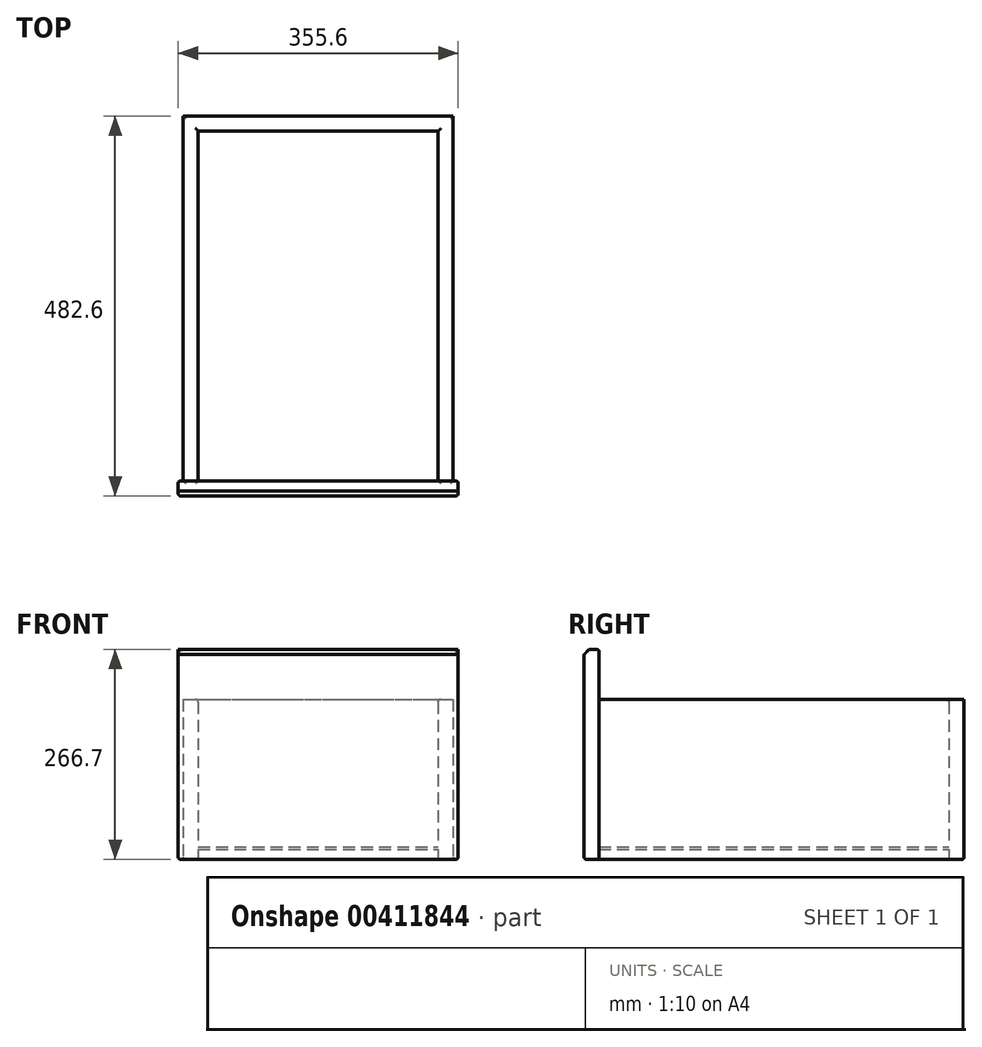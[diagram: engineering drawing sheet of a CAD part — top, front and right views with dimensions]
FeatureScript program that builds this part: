
annotation { "Feature Type Name" : "Feature", "Feature Type Description" : "" }
export const myFeature = defineFeature(function(context is Context, id is Id, definition is map)
    precondition{}
    {
        {
            var Q0;
            Q0=qCreatedBy(makeId("Top.planeOp"),FACE);
            var sketch = newSketch(context, id + "F0", { "sketchPlane" : qUnion([Q0])});
            skLineSegment(sketch, "E0.bottom", {"start": v(0, 0) * mm, "end": v(19.05, 0) * mm});
            skLineSegment(sketch, "E0.top", {"start": v(0, 463.55) * mm, "end": v(342.9, 463.55) * mm});
            skLineSegment(sketch, "E0.left", {"start": v(0, 0) * mm, "end": v(0, 463.55) * mm});
            skLineSegment(sketch, "E0.right", {"start": v(342.9, 0) * mm, "end": v(342.9, 463.55) * mm});
            skLineSegment(sketch, "E1.top", {"start": v(19.05, 444.5) * mm, "end": v(323.85, 444.5) * mm});
            skLineSegment(sketch, "E1.left", {"start": v(19.05, 0) * mm, "end": v(19.05, 444.5) * mm});
            skLineSegment(sketch, "E1.right", {"start": v(323.85, 0) * mm, "end": v(323.85, 444.5) * mm});
            skLineSegment(sketch, "E2.trimOffspring", {"start": v(323.85, 0) * mm, "end": v(342.9, 0) * mm});
            skSolve(sketch);
        }
        {
            var Q0;
            Q0=makeQuery(id+"F0.imprint","IMPRINT",FACE,{"disambiguationData":[TD([[makeQuery(id+"F0.imprint","IMPRINT",EDGE,{"derivedFrom":sQuery(id+"F0.wireOp",EDGE,"E0.bottom")}),1.0]])]});
            extrude(context, id + "F1", {"entities" : qUnion([Q0]), "depth" : 203.2 * mm});
        }
        {
            var Q0;
            Q0=qCreatedBy(makeId("Top.planeOp"),FACE);
            var sketch = newSketch(context, id + "F2", { "sketchPlane" : qUnion([Q0])});
            skLineSegment(sketch, "E3.bottom", {"start": v(-6.35, 0) * mm, "end": v(349.25, 0) * mm});
            skLineSegment(sketch, "E3.top", {"start": v(-6.35, -19.05) * mm, "end": v(349.25, -19.05) * mm});
            skLineSegment(sketch, "E3.left", {"start": v(-6.35, 0) * mm, "end": v(-6.35, -19.05) * mm});
            skLineSegment(sketch, "E3.right", {"start": v(349.25, 0) * mm, "end": v(349.25, -19.05) * mm});
            skSolve(sketch);
        }
        {
            var Q0;
            Q0 = qSketchRegion(id + "F2", true);
            extrude(context, id + "F3", {"entities" : qUnion([Q0]), "operationType" : NewBodyOperationType.ADD, "depth" : 266.7 * mm});
        }
        {
            var Q0;
            Q0=makeQuery(id+"F3.opExtrude","CAP_EDGE",EDGE,{"disambiguationData":[OSD([sQuery(id+"F2.wireOp",EDGE,"E3.top")])],"isStart":false});
            chamfer(context, id + "F4", {"entities" : qUnion([Q0]), "width" : 6.35 * mm, "tangentPropagation" : true});
        }
        {
            var Q0;
            Q0=makeQuery(id+"F3.opExtrude","SWEPT_EDGE",EDGE,{"disambiguationData":[OSD([sQuery(id+"F2.wireOp",EDGE,"E3.top"),sQuery(id+"F2.wireOp",EDGE,"E3.left")])]});
            var Q1;
            Q1=makeQuery(id+"F3.opExtrude","SWEPT_EDGE",EDGE,{"disambiguationData":[OSD([sQuery(id+"F2.wireOp",EDGE,"E3.bottom"),sQuery(id+"F2.wireOp",EDGE,"E3.left")])]});
            var Q2;
            {var subQ0=sQuery(id+"F2.wireOp",EDGE,"E3.bottom");var subQ2=sQuery(id+"F0.wireOp",EDGE,"E1.left");Q2=makeQuery(id+"F3.boolean.opBoolean","SPLIT",EDGE,{"disambiguationData":[TD([makeQuery(id+"F1.opExtrude","SWEPT_FACE",FACE,{"disambiguationData":[OSD([subQ2])]})])],"derivedFrom":makeQuery(id+"F3.opExtrude","CAP_EDGE",EDGE,{"disambiguationData":[OSD([subQ0])],"isStart":true})});}
            var Q3;
            Q3=makeQuery(id+"F3.opExtrude","CAP_EDGE",EDGE,{"disambiguationData":[OSD([sQuery(id+"F2.wireOp",EDGE,"E3.top")])],"isStart":true});
            var Q4;
            Q4=makeQuery(id+"F1.opExtrude","CAP_EDGE",EDGE,{"disambiguationData":[OSD([sQuery(id+"F0.wireOp",EDGE,"E0.left")])],"isStart":true});
            var Q5;
            Q5=makeQuery(id+"F1.opExtrude","CAP_EDGE",EDGE,{"disambiguationData":[OSD([sQuery(id+"F0.wireOp",EDGE,"E1.left")])],"isStart":true});
            var Q6;
            Q6=makeQuery(id+"F1.opExtrude","CAP_EDGE",EDGE,{"disambiguationData":[OSD([sQuery(id+"F0.wireOp",EDGE,"E0.top")])],"isStart":true});
            var Q7;
            Q7=makeQuery(id+"F1.opExtrude","CAP_EDGE",EDGE,{"disambiguationData":[OSD([sQuery(id+"F0.wireOp",EDGE,"E1.top")])],"isStart":true});
            var Q8;
            Q8=makeQuery(id+"F1.opExtrude","CAP_EDGE",EDGE,{"disambiguationData":[OSD([sQuery(id+"F0.wireOp",EDGE,"E1.right")])],"isStart":true});
            var Q9;
            Q9=makeQuery(id+"F1.opExtrude","CAP_EDGE",EDGE,{"disambiguationData":[OSD([sQuery(id+"F0.wireOp",EDGE,"E0.right")])],"isStart":true});
            var Q10;
            Q10=makeQuery(id+"F3.opExtrude","SWEPT_EDGE",EDGE,{"disambiguationData":[OSD([sQuery(id+"F2.wireOp",EDGE,"E3.bottom"),sQuery(id+"F2.wireOp",EDGE,"E3.right")])]});
            var Q11;
            Q11=makeQuery(id+"F3.opExtrude","SWEPT_EDGE",EDGE,{"disambiguationData":[OSD([sQuery(id+"F2.wireOp",EDGE,"E3.top"),sQuery(id+"F2.wireOp",EDGE,"E3.right")])]});
            var Q12;
            Q12=makeQuery(id+"F1.opExtrude","CAP_EDGE",EDGE,{"disambiguationData":[OSD([sQuery(id+"F0.wireOp",EDGE,"E1.left")])],"isStart":false});
            var Q13;
            Q13=makeQuery(id+"F1.opExtrude","CAP_EDGE",EDGE,{"disambiguationData":[OSD([sQuery(id+"F0.wireOp",EDGE,"E1.top")])],"isStart":false});
            var Q14;
            Q14=makeQuery(id+"F1.opExtrude","CAP_EDGE",EDGE,{"disambiguationData":[OSD([sQuery(id+"F0.wireOp",EDGE,"E1.right")])],"isStart":false});
            var Q15;
            Q15=makeQuery(id+"F3.opExtrude","CAP_EDGE",EDGE,{"disambiguationData":[OSD([sQuery(id+"F2.wireOp",EDGE,"E3.left")])],"isStart":true});
            var Q16;
            Q16=makeQuery(id+"F3.opExtrude","CAP_EDGE",EDGE,{"disambiguationData":[OSD([sQuery(id+"F2.wireOp",EDGE,"E3.right")])],"isStart":true});
            var Q17;
            {var subQ1=sQuery(id+"F2.wireOp",EDGE,"E3.bottom");var subQ2=sQuery(id+"F0.wireOp",EDGE,"E0.right");Q17=makeQuery(id+"F3.boolean.opBoolean","SPLIT",EDGE,{"disambiguationData":[TD([makeQuery(id+"F1.opExtrude","SWEPT_FACE",FACE,{"disambiguationData":[OSD([subQ2])]})])],"derivedFrom":makeQuery(id+"F3.opExtrude","CAP_EDGE",EDGE,{"disambiguationData":[OSD([subQ1])],"isStart":true})});}
            var Q18;
            {var subQ0=sQuery(id+"F2.wireOp",EDGE,"E3.bottom");var subQ1=sQuery(id+"F0.wireOp",EDGE,"E0.left");Q18=makeQuery(id+"F3.boolean.opBoolean","SPLIT",EDGE,{"disambiguationData":[TD([makeQuery(id+"F1.opExtrude","SWEPT_FACE",FACE,{"disambiguationData":[OSD([subQ1])]})])],"derivedFrom":makeQuery(id+"F3.opExtrude","CAP_EDGE",EDGE,{"disambiguationData":[OSD([subQ0])],"isStart":true})});}
            var Q19;
            Q19=makeQuery(id+"F3.opExtrude","CAP_EDGE",EDGE,{"disambiguationData":[OSD([sQuery(id+"F2.wireOp",EDGE,"E3.bottom")])],"isStart":false});
            fillet(context, id + "F5", {"entities" : qUnion([Q0, Q1, Q2, Q3, Q4, Q5, Q6, Q7, Q8, Q9, Q10, Q11, Q12, Q13, Q14, Q15, Q16, Q17, Q18, Q19]), "radius" : 3.17 * mm, "tangentPropagation" : true, "allowEdgeOverflow" : false});
        }
        {
            var Q0;
            Q0=qCreatedBy(makeId("Top.planeOp"),FACE);
            var sketch = newSketch(context, id + "F6", { "sketchPlane" : qUnion([Q0])});
            skLineSegment(sketch, "E4.bottom", {"start": v(19.05, 0) * mm, "end": v(323.85, 0) * mm});
            skLineSegment(sketch, "E4.top", {"start": v(19.05, 444.5) * mm, "end": v(323.85, 444.5) * mm});
            skLineSegment(sketch, "E4.left", {"start": v(19.05, 0) * mm, "end": v(19.05, 444.5) * mm});
            skLineSegment(sketch, "E4.right", {"start": v(323.85, 0) * mm, "end": v(323.85, 444.5) * mm});
            skSolve(sketch);
        }
        {
            var Q0;
            Q0 = qSketchRegion(id + "F6", true);
            extrude(context, id + "F7", {"entities" : qUnion([Q0]), "operationType" : NewBodyOperationType.ADD, "depth" : 15.88 * mm});
        }
        {
            var Q0;
            Q0 = qSketchRegion(id + "F6", true);
            extrude(context, id + "F8", {"entities" : qUnion([Q0]), "operationType" : NewBodyOperationType.REMOVE, "depth" : 12.7 * mm});
        }
    });
